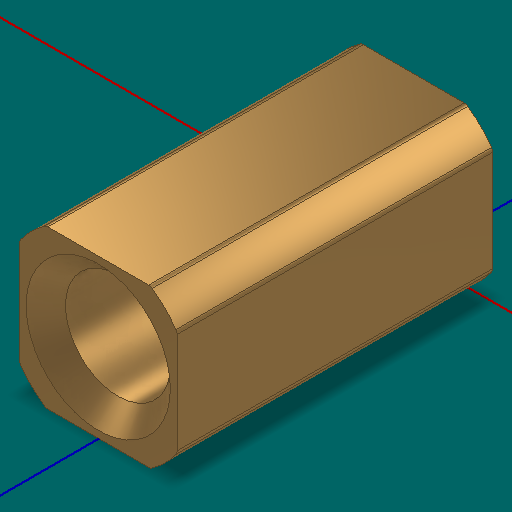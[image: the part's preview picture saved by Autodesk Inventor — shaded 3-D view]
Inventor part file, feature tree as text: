
AUTODESK INVENTOR PART (.ipt)
format: ipt  version: 2025 (Build 290162000, 162)  size: 165,888 bytes
history: native  units: in
note: dims shown in document units (in); Inventor stores cm internally (conversion verified against a paired STEP export)
features: other x3, sketch x2
ambient origin geometry x8: Origin, YZ Plane, XZ Plane, XY Plane, X Axis, Y Axis, Z Axis, Center Point
bodies: Solid1 (feature_tree)
feature tree (5):
  other  "HS Shaft Adapter Circle.ipt"
  other  "Solid1::HS Shaft Adapter Circle.ipt"
  other  "TaggingFeature1"
  sketch  "Sketch1"  dims[d0=0.3937in]
  sketch  "Sketch2"
